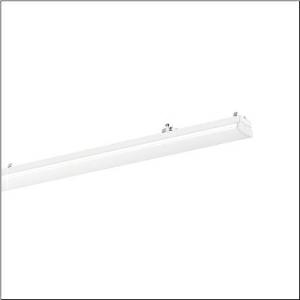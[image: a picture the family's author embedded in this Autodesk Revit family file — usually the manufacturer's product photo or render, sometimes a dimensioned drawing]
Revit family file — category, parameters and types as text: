
# Revit family: licross_11_recessed_opal_mo_51te1d7n48xg
name_source: partatom
category: Lighting Fixtures
units: mm (PartAtom-declared; Revit-internal decimal feet)

## family parameters
Cut with Voids When Loaded = No
Host = Face
Light Source = No
Part Type = Normal
Room Calculation Point = No
Round Connector Dimension = Use Diameter
Shared = No

## types (1)
- Licross 11 recessed opal MO (1 x LED, 8490 lm, 48.5 W, 4000K)
    Apparent Load = 49 VA
    CIE Flux Codes = 44 73 91 87 100
    Color Rendering = 80
    Color Temperature = 4000K
    Default Elevation = 1800 mm
    Description = Licross 11 recessed opal MO, luminaire insert, of sheet steel, coil coated, white, length: 1.500mm, width: 76mm, height: 87mm, LED rated luminous flux: 8.490lm, light colour: 840, SDCM (Standard Deviation of Colour Matching)MacAdam ≤ 2 SDCM (initial), control gear: ON/OFF, with plug, 3-pole, with phase selection, mains connection: 220..240V, AC, 50/60Hz, rated input power: 49W, internal wiring halogen-free, primary optical cover: cover, of PMMA, light emission: direct with ceiling illumination distribution, primary light characteristic: symmetric, protection rating (complete): IP54, insulation class (complete): insulation class I (protective earthing), certification: CE, ENEC, VDE, UKCA, protection symbol: D if used in an environment with non-conductive dust loads with corresponding accessories, impact resistance: IK06, permissible ambient temperature for indoor applications: -35..+35°C, corresponds to IFS (International Featured Standards) requirements for safety and quality in the food industry, reducing of maximum allowable ambient temperature of 5°C with ceiling mounting, The light source and the operating device comply with the requirements of the Ecodesign Regulation (EU) 2019/2020 and are replaceable in accordance with this regulation, packaging unit: 1 piece
    Height = 83 mm
    Lamp = 1 x LED
    Lamp Light Flux = 8490 lm
    Lamp Power = 48.5 W
    Lamp count = 1
    Length = 1500 mm
    Luminous efficacy = 175 lm/W
    Manufacturer = Siteco
    ModVariant = No
    Model = 51TE1D7N48XG
    Mounting Place = Ceiling
    Mounting Type = Pendant
    Number of Poles = 1
    OnlyDefault = Yes
    Power Factor = 1
    Product Name = Licross 11 recessed opal MO
    Product group = luminaire insert | ceiling pendant
    ProductGroupID = 901
    Protection Class = Protection class I
    Protection Degree = IP 54
    RLX_Detail_Level = 1
    RLX_Emergency_Light_Flux = 0 lm
    RLX_Emergency_Type = 0
    RLX_Emergency_Type_DB = No
    RlxData = <blob elided: 23385 chars, md5=199820ed>
    Socket = socket
    Standby Power = 0 W
    System Light Flux = 8490 lm
    System Power = 49 W
    Type Comments = Product without accessories
    Type Image = l_1313666.jpg
    URL = http://relux.com
    VarID = ---
    Voltage = 0 V
    Weight = 0.00 kg
    Width = 76 mm

## geometry (parser evidence)
native form markers: Blend x4, Sweep x15
no freeform markers — native parametric forms only
